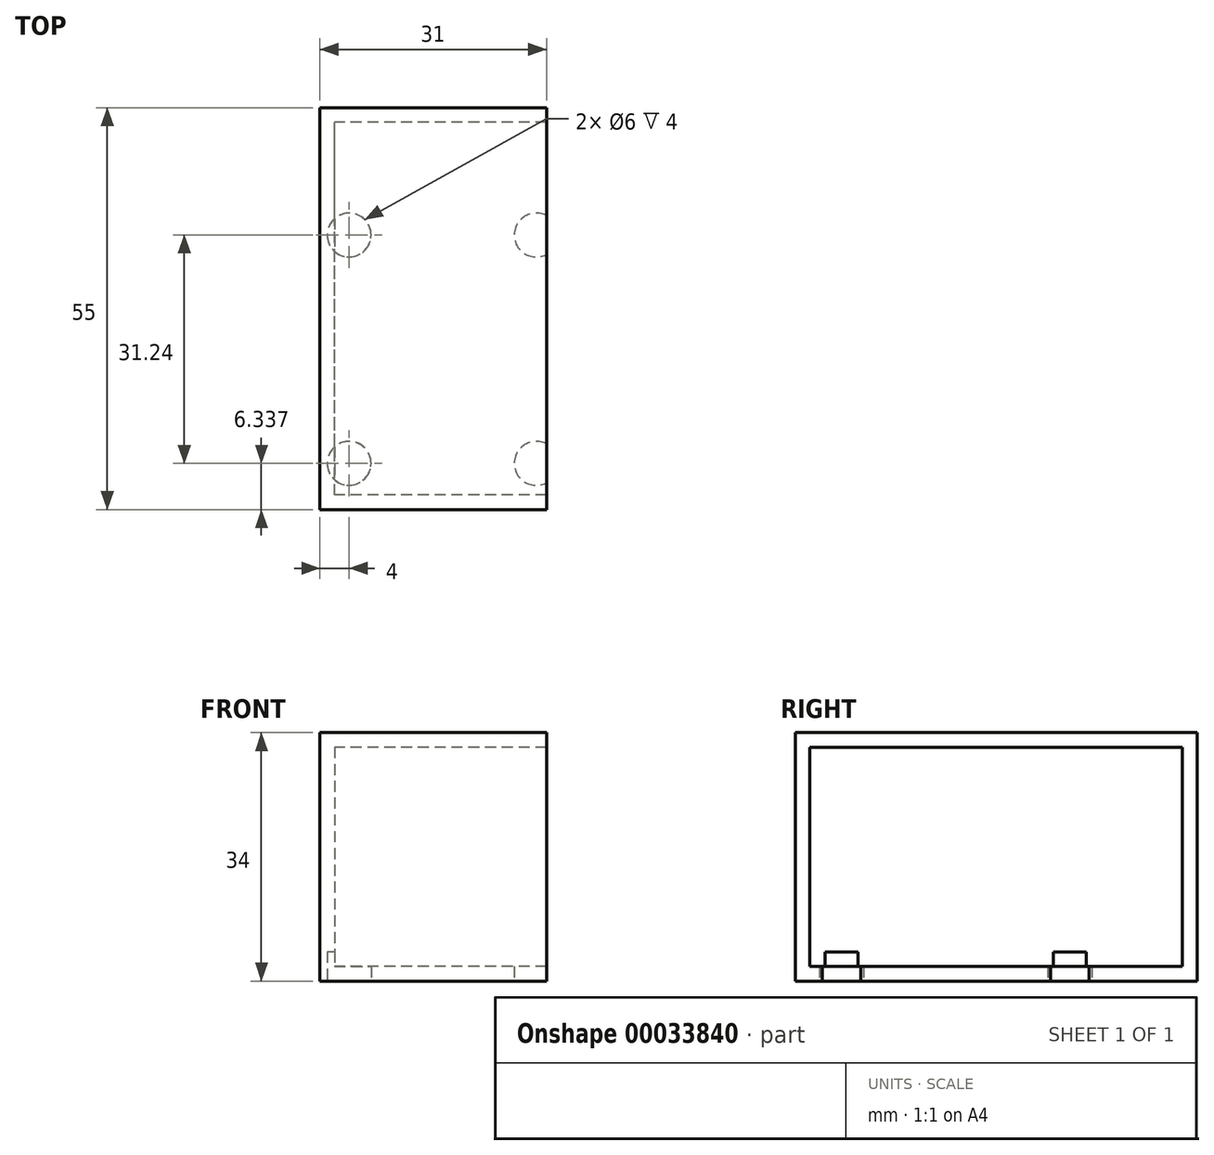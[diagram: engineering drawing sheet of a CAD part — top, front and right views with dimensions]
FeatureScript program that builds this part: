
annotation { "Feature Type Name" : "Feature", "Feature Type Description" : "" }
export const myFeature = defineFeature(function(context is Context, id is Id, definition is map)
    precondition{}
    {
        {
            var Q0;
            Q0=qCreatedBy(makeId("Top.planeOp"),FACE);
            var sketch = newSketch(context, id + "F0", { "sketchPlane" : qUnion([Q0])});
            skLineSegment(sketch, "E0.rect.bottom", {"start": v(15.5, -27.5) * mm, "end": v(-15.5, -27.5) * mm});
            skLineSegment(sketch, "E0.rect.top", {"start": v(15.5, 27.5) * mm, "end": v(-15.5, 27.5) * mm});
            skLineSegment(sketch, "E0.rect.left", {"start": v(15.5, -27.5) * mm, "end": v(15.5, 27.5) * mm});
            skLineSegment(sketch, "E0.rect.right", {"start": v(-15.5, -27.5) * mm, "end": v(-15.5, 27.5) * mm});
            skPoint(sketch, "E0.rect.middle", {"position": v(0, 0) * mm});
            skSolve(sketch);
        }
        {
            var Q0;
            Q0=makeQuery(id+"F0.imprint","IMPRINT",FACE,{"disambiguationData":[TD([[makeQuery(id+"F0.imprint","IMPRINT",EDGE,{"derivedFrom":sQuery(id+"F0.wireOp",EDGE,"E0.rect.bottom")}),-1.0]])]});
            extrude(context, id + "F1", {"entities" : qUnion([Q0]), "depth" : 34 * mm});
        }
        {
            var Q0;
            Q0=makeQuery(id+"F1.opExtrude","SWEPT_FACE",FACE,{"disambiguationData":[OSD([sQuery(id+"F0.wireOp",EDGE,"E0.rect.left")])]});
            shell(context, id + "F2", {"entities" : qUnion([Q0]), "thickness" : 2 * mm});
        }
        {
            var Q0;
            Q0=makeQuery(id+"F1.opExtrude","CAP_FACE",FACE,{"disambiguationData":[OSD([sQuery(id+"F0.wireOp",EDGE,"E0.rect.bottom"),sQuery(id+"F0.wireOp",EDGE,"E0.rect.top"),sQuery(id+"F0.wireOp",EDGE,"E0.rect.left"),sQuery(id+"F0.wireOp",EDGE,"E0.rect.right")])],"isStart":true});
            var sketch = newSketch(context, id + "F3", { "sketchPlane" : qUnion([Q0])});
            skCircle(sketch, "E1.0.1.0", {"center": v(-11.5, -10.08) * mm, "radius": 3 * mm});
            skLineSegment(sketch, "E2", {"start": v(-11.5, -29.45) * mm, "end": v(-11.5, 30.42) * mm, "construction": true});
            skCircle(sketch, "E3.0.1.0", {"center": v(-11.5, 21.16) * mm, "radius": 3 * mm});
            skCircle(sketch, "E3.1.0.0", {"center": v(14.1, -10.08) * mm, "radius": 3 * mm});
            skCircle(sketch, "E3.1.1.0", {"center": v(14.1, 21.16) * mm, "radius": 3 * mm});
            skLineSegment(sketch, "E3.direction1", {"start": v(-11.5, -10.08) * mm, "end": v(14.1, -10.08) * mm, "construction": true});
            skLineSegment(sketch, "E3.direction2", {"start": v(-11.5, -10.08) * mm, "end": v(-11.5, 21.16) * mm, "construction": true});
            skSolve(sketch);
        }
        {
            var Q0;
            Q0 = qSketchRegion(id + "F3", true);
            extrude(context, id + "F4", {"entities" : qUnion([Q0]), "operationType" : NewBodyOperationType.REMOVE, "oppositeDirection" : true, "depth" : 4 * mm});
        }
    });
